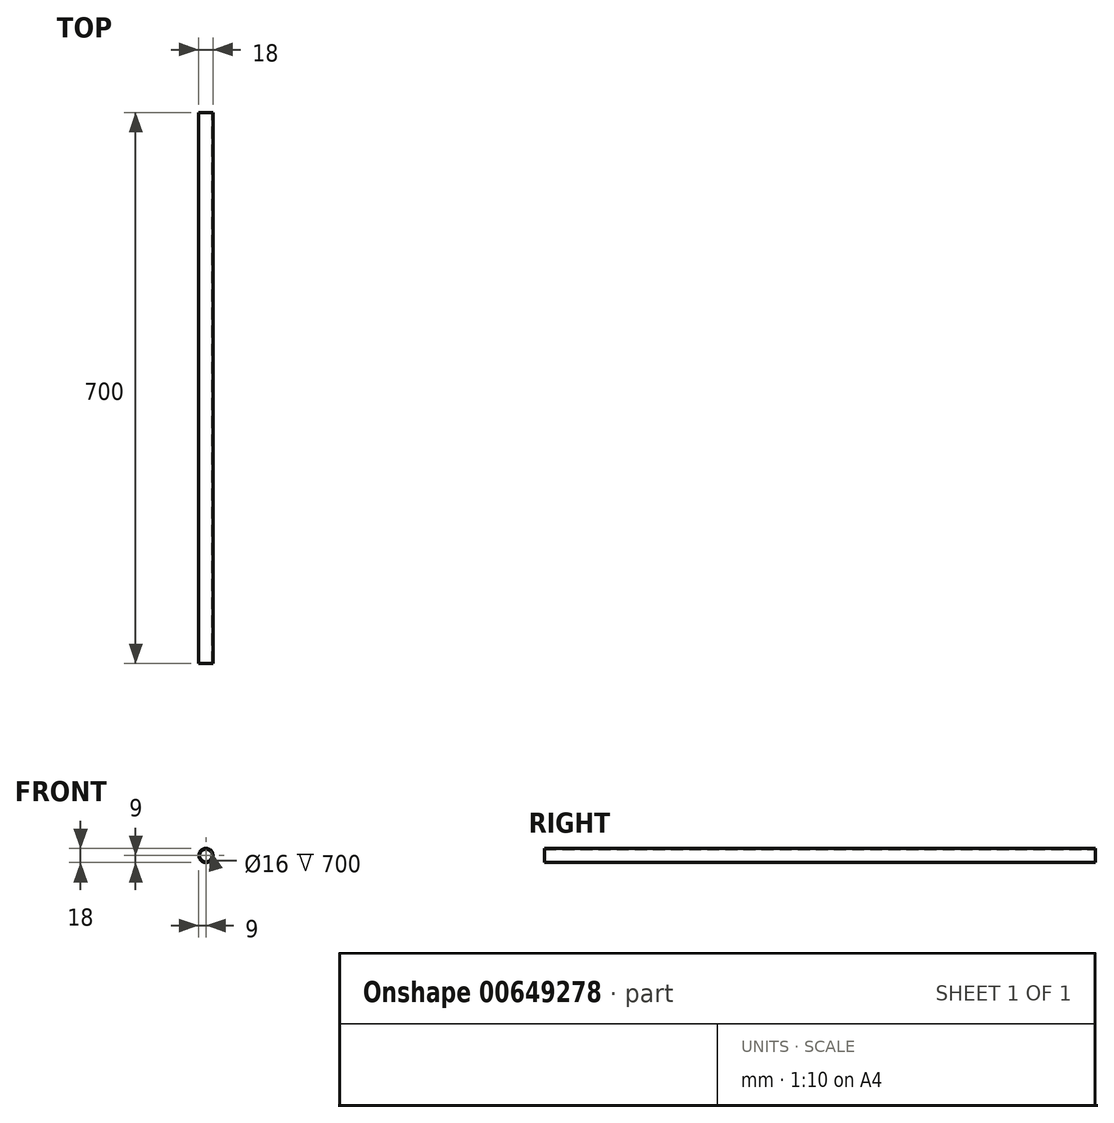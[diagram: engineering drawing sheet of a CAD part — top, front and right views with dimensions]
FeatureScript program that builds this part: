
annotation { "Feature Type Name" : "Feature", "Feature Type Description" : "" }
export const myFeature = defineFeature(function(context is Context, id is Id, definition is map)
    precondition{}
    {
        {
            var Q0;
            Q0=qCreatedBy(makeId("Front.planeOp"),FACE);
            var sketch = newSketch(context, id + "F0", { "sketchPlane" : qUnion([Q0])});
            skCircle(sketch, "E0", {"center": v(0, 0) * mm, "radius": 9 * mm});
            skCircle(sketch, "E1", {"center": v(0, 0) * mm, "radius": 8 * mm});
            skSolve(sketch);
        }
        {
            var Q0;
            Q0=qSketchRegion(id+"F0",true);
            extrude(context, id + "F1", {"entities" : qUnion([Q0]), "depth" : 700 * mm, "offsetDistance" : 25 * mm});
        }
    });
